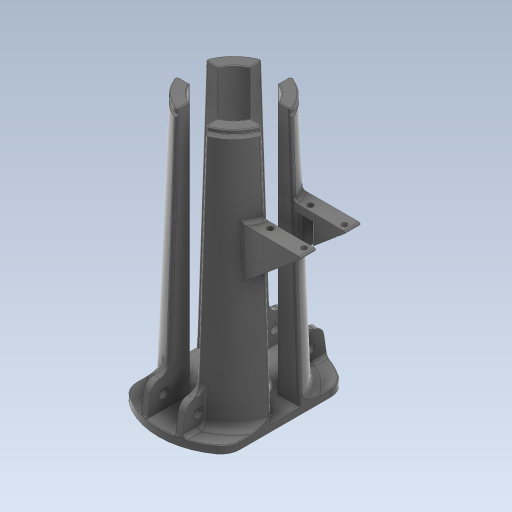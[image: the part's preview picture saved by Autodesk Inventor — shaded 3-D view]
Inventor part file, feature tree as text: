
AUTODESK INVENTOR PART (.ipt)
format: ipt  version: 2023 (Build 270158000, 158)  size: 1,636,864 bytes
history: native  units: mm
features: fillet x12, sketch x8, extrude x6, mirror x4, hole x4, draft x3, plane x3, projected_geometry x3, revolve x1, chamfer x1
ambient origin geometry x8: Origin, YZ Plane, XZ Plane, XY Plane, X Axis, Y Axis, Z Axis, Center Point
bodies: Solid1 (feature_tree)
feature tree (45):
  extrude  "Extrusion1"  Depth=35.75mm
  extrude  "Extrusion2"  Depth=80.0mm
  extrude  "Extrusion3"  Depth=27.5mm
  draft  "FaceDraft1"
  fillet  "Fillet1"  Radius=4.0mm
  fillet  "Fillet2"  Radius=27.8mm
  fillet  "Fillet3"  Radius=4.0mm
  plane  "Work Plane1"
  sketch  "Sketch5"  dims[d17=0.349066mm d18=4.0mm]
  revolve  "Revolution1"  [1 undecoded]
  extrude  "Extrusion4"  Depth=10.0mm
  extrude  "Extrusion5"  TaperAngle=45.0deg  [1 undecoded]
  draft  "FaceDraft2"
  mirror  "Mirror1"
  mirror  "Mirror2"
  fillet  "Fillet5"  [1 undecoded]
  fillet  "Fillet6"  [1 undecoded]
  fillet  "Fillet8"  Radius=24.7mm
  fillet  "Fillet9"  Radius=23.2mm
  chamfer  "Chamfer1"  Distance=11.0mm
  plane  "Work Plane2"
  extrude  "Extrusion6"  Depth=0.5mm TaperAngle=0.0deg
  draft  "FaceDraft4"
  plane  "Work Plane3"
  sketch  "Sketch12"  dims[d29=13.2mm d32=11.0mm d33=15.2mm d34=0.0mm d35=15.2mm d36=4.65mm d37=6.6mm d38=7.3mm d39=0.0mm d40=0.0mm d41=1.396263mm d43=5.5mm d44=2.0mm d46=0.5mm d47=1.0mm d48=0.3mm d49=2.0mm d50=45.0deg d51=-96.8mm d54=27.94mm d55=51.673462mm d56=30.94mm d57=2.98mm d58=3.225mm d60=30.265mm d62=18.0mm d65=30.94mm d66=0.0mm d70=15.54mm d75=8.726646mm d76=4.0mm d77=3.1mm d78=6.0mm d79=6.0mm d80=10.0mm d81=90.0deg d82=8.0mm d83=20.594885mm d84=6.5mm d85=6.0mm d86=5.5mm d87=10.0mm d88=90.0deg d89=8.0mm d90=20.594885mm d91=3.1mm d92=6.0mm d93=6.0mm d94=10.0mm d95=90.0deg d96=8.0mm d97=20.594885mm d98=6.5mm d99=6.0mm d100=5.5mm d101=10.0mm d102=90.0deg d103=30.0mm d104=90.0deg d105=2.0mm d107=2.0mm d108=2.0mm d109=1.75mm d110=0.7mm d111=0.5mm d112=32.364215mm]
  hole  "Hole1"  [1 undecoded]
  hole  "Hole2"  [1 undecoded]
  mirror  "Mirror3"
  hole  "Hole3"  [1 undecoded]
  hole  "Hole4"  [1 undecoded]
  mirror  "Mirror4"
  fillet  "Fillet12"  [1 undecoded]
  fillet  "Fillet14"  Radius=1.396263mm
  fillet  "Fillet15"  Radius=5.5mm
  fillet  "Fillet16"  Radius=2.0mm
  fillet  "Fillet17"  Radius=0.5mm
  sketch  "Sketch1"  dims[d0=7.5mm d1=7.0mm d2=7.5mm d3=0.0mm d4=7.0mm d5=28.73603mm d6=35.75mm]
  sketch  "Sketch2"  dims[d7=135.0mm d8=0.0mm d9=80.0mm]
  sketch  "Sketch3"  dims[d10=55.0mm d11=27.5mm d12=4.0mm d13=0.0mm d14=27.8mm d15=4.0mm d16=0.0mm]
  sketch  "Sketch6"  dims[d19=10.0mm d20=1.2mm]
  sketch  "Sketch8"  dims[d21=-3.0mm d22=45.0deg d23=45.0deg d25=90.0deg d26=24.7mm d27=23.2mm]
  projected_geometry  "Projected Loop1"
  sketch  "Sketch9"  dims[d28=0.0mm]
  projected_geometry  "Projected Loop4"
  projected_geometry  "Projected Loop5"
note: 9 required parameter values undecoded (feature->parameter linkage not recoverable at this tier; creation-order binding heuristic only, values carry confidence <= 0.55)